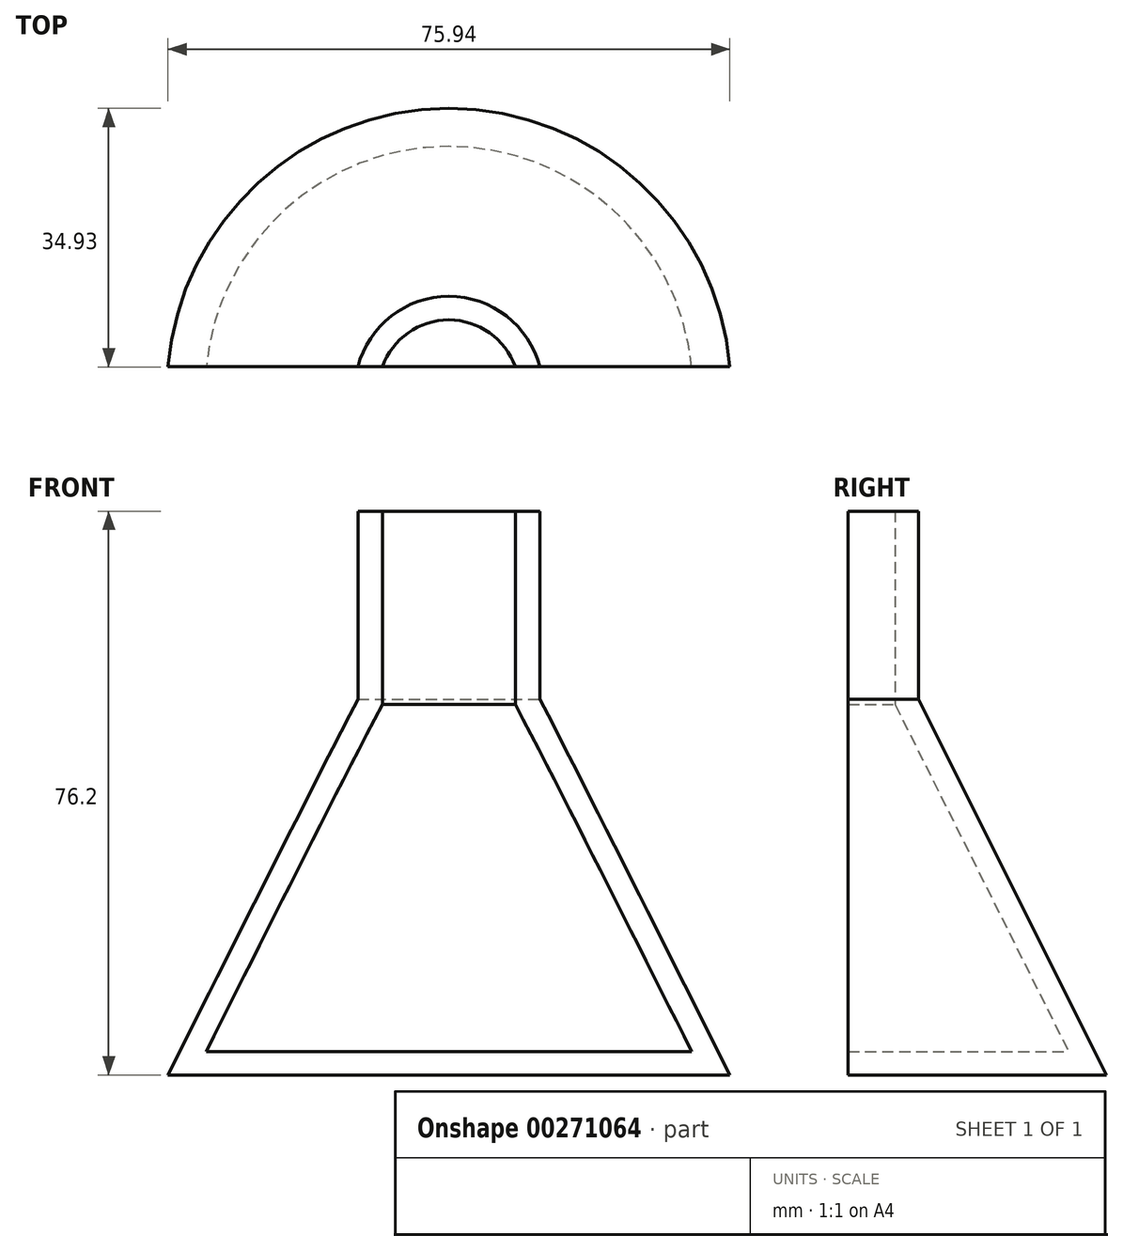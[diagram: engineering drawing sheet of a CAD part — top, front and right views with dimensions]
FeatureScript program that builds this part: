
annotation { "Feature Type Name" : "Feature", "Feature Type Description" : "" }
export const myFeature = defineFeature(function(context is Context, id is Id, definition is map)
    precondition{}
    {
        {
            var Q0;
            Q0=qCreatedBy(makeId("Front.planeOp"),FACE);
            var sketch = newSketch(context, id + "F0", { "sketchPlane" : qUnion([Q0])});
            skLineSegment(sketch, "E0", {"start": v(0, 0) * mm, "end": v(0, 50.8) * mm});
            skLineSegment(sketch, "E1", {"start": v(0, 50.8) * mm, "end": v(12.7, 50.8) * mm});
            skLineSegment(sketch, "E2", {"start": v(0, 0) * mm, "end": v(38.1, 0) * mm});
            skLineSegment(sketch, "E3", {"start": v(12.7, 50.8) * mm, "end": v(38.1, 0) * mm});
            skSolve(sketch);
        }
        {
            var Q0;
            Q0=makeQuery(id+"F0.imprint","IMPRINT",FACE,{"disambiguationData":[TD([[makeQuery(id+"F0.imprint","IMPRINT",EDGE,{"derivedFrom":sQuery(id+"F0.wireOp",EDGE,"E0")}),-1.0]])]});
            var Q1;
            Q1=sQuery(id+"F0.wireOp",EDGE,"E0");
            revolve(context, id + "F1", {"entities" : qUnion([Q0]), "axis" : qUnion([Q1]), "revolveType" : RevolveType.ONE_DIRECTION, "angle" : 180 * degree});
        }
        {
            var Q0;
            Q0=makeQuery(id+"F1.opRevolve","SWEPT_FACE",FACE,{"disambiguationData":[OSD([sQuery(id+"F0.wireOp",EDGE,"E1")])]});
            var sketch = newSketch(context, id + "F2", { "sketchPlane" : qUnion([Q0])});
            skCircle(sketch, "E4", {"center": v(0, 0) * mm, "radius": 12.7 * mm});
            skSolve(sketch);
        }
        {
            var Q0;
            Q0=makeQuery(id+"F2.imprint","IMPRINT",FACE,{"disambiguationData":[TD([[makeQuery(id+"F2.imprint","IMPRINT",EDGE,{"derivedFrom":sQuery(id+"F2.wireOp",EDGE,"E4")}),-1.0]])]});
            extrude(context, id + "F3", {"entities" : qUnion([Q0]), "operationType" : NewBodyOperationType.ADD, "depth" : 25.4 * mm});
        }
        {
            var Q0;
            Q0=makeQuery(id+"F3.opExtrude","CAP_FACE",FACE,{"disambiguationData":[OSD([sQuery(id+"F2.wireOp",EDGE,"E4")])],"isStart":false});
            shell(context, id + "F4", {"entities" : qUnion([Q0]), "thickness" : 3.17 * mm});
        }
        {
            var Q0;
            {var subQ0=sQuery(id+"F0.wireOp",EDGE,"E1");Q0=makeQuery(id+"F3.boolean.opBoolean","MERGE",FACE,{"derivedFrom":[makeQuery(id+"F1.opRevolve","CAP_FACE",FACE,{"disambiguationData":[OSD([sQuery(id+"F0.wireOp",EDGE,"E0"),subQ0,sQuery(id+"F0.wireOp",EDGE,"E2"),sQuery(id+"F0.wireOp",EDGE,"E3")])],"isStart":false}),makeQuery(id+"F3.opExtrude","SWEPT_FACE",FACE,{"disambiguationData":[OSD([subQ0])]})]});}
            extrude(context, id + "F5", {"entities" : qUnion([Q0]), "operationType" : NewBodyOperationType.REMOVE, "oppositeDirection" : true, "depth" : 3.17 * mm});
        }
    });
